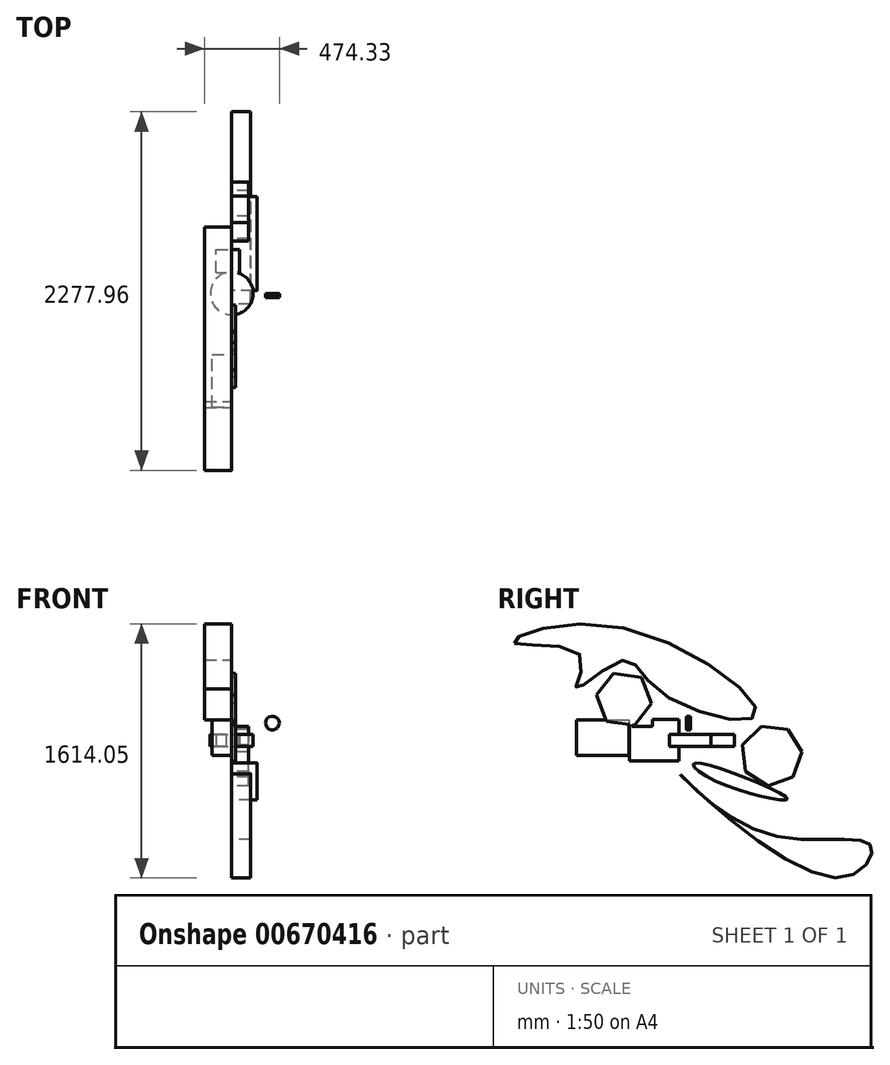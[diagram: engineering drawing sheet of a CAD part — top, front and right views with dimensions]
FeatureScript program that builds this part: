
annotation { "Feature Type Name" : "Feature", "Feature Type Description" : "" }
export const myFeature = defineFeature(function(context is Context, id is Id, definition is map)
    precondition{}
    {
        {
            var Q0;
            Q0=qCreatedBy(makeId("Top.planeOp"),FACE);
            var sketch = newSketch(context, id + "F0", { "sketchPlane" : qUnion([Q0])});
            skCircle(sketch, "E0", {"center": v(0, 0) * mm, "radius": 136.41 * mm});
            skLineSegment(sketch, "E1.bottom", {"start": v(-99.12, 131) * mm, "end": v(49.66, 131) * mm});
            skLineSegment(sketch, "E1.top", {"start": v(-99.12, 278.74) * mm, "end": v(49.66, 278.74) * mm});
            skLineSegment(sketch, "E1.left", {"start": v(-99.12, 131) * mm, "end": v(-99.12, 278.74) * mm});
            skLineSegment(sketch, "E1.right", {"start": v(49.66, 131) * mm, "end": v(49.66, 278.74) * mm});
            skSolve(sketch);
        }
        {
            var Q0;
            Q0=makeQuery(id+"F0.imprint","IMPRINT",FACE,{"disambiguationData":[TD([[makeQuery(id+"F0.imprint","IMPRINT",EDGE,{"derivedFrom":sQuery(id+"F0.wireOp",EDGE,"E1.top")}),-1.0]])]});
            var Q1;
            {var subQ0=sQuery(id+"F0.wireOp",EDGE,"E1.bottom");var subQ1=sQuery(id+"F0.wireOp",EDGE,"E0");var subQ2=makeQuery(id+"F0.imprint","INTERSECT",VERTEX,{"disambiguationData":[OD(0.0)],"derivedFrom":[subQ1,subQ0]});Q1=makeQuery(id+"F0.imprint","IMPRINT",FACE,{"disambiguationData":[TD([[makeQuery(id+"F0.imprint","IMPRINT",EDGE,{"disambiguationData":[TD([[subQ2,1.0]])],"derivedFrom":subQ1}),1.0]])]});}
            var Q2;
            {var subQ0=sQuery(id+"F0.wireOp",EDGE,"E1.bottom");var subQ1=sQuery(id+"F0.wireOp",EDGE,"E0");var subQ2=makeQuery(id+"F0.imprint","INTERSECT",VERTEX,{"disambiguationData":[OD(0.0)],"derivedFrom":[subQ1,subQ0]});Q2=makeQuery(id+"F0.imprint","IMPRINT",FACE,{"disambiguationData":[TD([[makeQuery(id+"F0.imprint","IMPRINT",EDGE,{"disambiguationData":[TD([[subQ2,-1.0]])],"derivedFrom":subQ1}),1.0]])]});}
            extrude(context, id + "F1", {"entities" : qUnion([Q0, Q1, Q2]), "depth" : 76.2 * mm, "offsetDistance" : 25.4 * mm});
        }
        {
            var Q0;
            Q0=qCreatedBy(makeId("Right.planeOp"),FACE);
            var sketch = newSketch(context, id + "F2", { "sketchPlane" : qUnion([Q0])});
            skLineSegment(sketch, "E2.bottom", {"start": v(-240.28, 128.57) * mm, "end": v(-370.37, 128.57) * mm});
            skLineSegment(sketch, "E2.top", {"start": v(-240.28, 215.65) * mm, "end": v(-370.37, 215.65) * mm});
            skLineSegment(sketch, "E2.left", {"start": v(-240.28, 128.57) * mm, "end": v(-240.28, 215.65) * mm});
            skLineSegment(sketch, "E2.right", {"start": v(-370.37, 128.57) * mm, "end": v(-370.37, 215.65) * mm});
            skLineSegment(sketch, "E3.bottom", {"start": v(-73.44, -92) * mm, "end": v(-385.92, -92) * mm});
            skLineSegment(sketch, "E3.top", {"start": v(-73.44, 172) * mm, "end": v(-385.92, 172) * mm});
            skLineSegment(sketch, "E3.left", {"start": v(-73.44, -92) * mm, "end": v(-73.44, 172) * mm});
            skLineSegment(sketch, "E3.right", {"start": v(-385.92, -92) * mm, "end": v(-385.92, 172) * mm});
            skSolve(sketch);
        }
        {
            var Q0;
            {var subQ1=sQuery(id+"F2.wireOp",EDGE,"E2.bottom");Q0=makeQuery(id+"F2.imprint","IMPRINT",FACE,{"disambiguationData":[TD([[makeQuery(id+"F2.imprint","IMPRINT",EDGE,{"derivedFrom":subQ1}),1.0]])]});}
            extrude(context, id + "F3", {"entities" : qUnion([Q0]), "operationType" : NewBodyOperationType.ADD, "depth" : 25.4 * mm, "offsetDistance" : 25.4 * mm});
        }
        {
            var Q0;
            Q0=qCreatedBy(makeId("Front.planeOp"),FACE);
            var sketch = newSketch(context, id + "F4", { "sketchPlane" : qUnion([Q0])});
            skCircle(sketch, "E4.cCircle", {"center": v(257.8, 149.5) * mm, "radius": 43.18 * mm, "construction": true});
            skLineSegment(sketch, "E4.0", {"start": v(267.09, 192.35) * mm, "end": v(281.18, 186.59) * mm});
            skLineSegment(sketch, "E4.1", {"start": v(281.18, 186.59) * mm, "end": v(292.46, 176.35) * mm});
            skLineSegment(sketch, "E4.2", {"start": v(292.46, 176.35) * mm, "end": v(299.55, 162.88) * mm});
            skLineSegment(sketch, "E4.3", {"start": v(299.55, 162.88) * mm, "end": v(301.61, 147.8) * mm});
            skLineSegment(sketch, "E4.4", {"start": v(301.61, 147.8) * mm, "end": v(298.38, 132.9) * mm});
            skLineSegment(sketch, "E4.5", {"start": v(298.38, 132.9) * mm, "end": v(290.26, 120.03) * mm});
            skLineSegment(sketch, "E4.6", {"start": v(290.26, 120.03) * mm, "end": v(278.22, 110.7) * mm});
            skLineSegment(sketch, "E4.7", {"start": v(278.22, 110.7) * mm, "end": v(263.72, 106.05) * mm});
            skLineSegment(sketch, "E4.8", {"start": v(263.72, 106.05) * mm, "end": v(248.5, 106.65) * mm});
            skLineSegment(sketch, "E4.9", {"start": v(248.5, 106.65) * mm, "end": v(234.4, 112.4) * mm});
            skLineSegment(sketch, "E4.10", {"start": v(234.4, 112.4) * mm, "end": v(223.13, 122.64) * mm});
            skLineSegment(sketch, "E4.11", {"start": v(223.13, 122.64) * mm, "end": v(216.04, 136.12) * mm});
            skLineSegment(sketch, "E4.12", {"start": v(216.04, 136.12) * mm, "end": v(213.98, 151.2) * mm});
            skLineSegment(sketch, "E4.13", {"start": v(213.98, 151.2) * mm, "end": v(217.2, 166.09) * mm});
            skLineSegment(sketch, "E4.14", {"start": v(217.2, 166.09) * mm, "end": v(225.33, 178.97) * mm});
            skLineSegment(sketch, "E4.15", {"start": v(225.33, 178.97) * mm, "end": v(237.37, 188.3) * mm});
            skLineSegment(sketch, "E4.16", {"start": v(237.37, 188.3) * mm, "end": v(251.87, 192.94) * mm});
            skLineSegment(sketch, "E4.17", {"start": v(251.87, 192.94) * mm, "end": v(267.09, 192.35) * mm});
            skPoint(sketch, "E4.0.midPoint", {"position": v(274.13, 189.47) * mm});
            skCircle(sketch, "E5.cCircle", {"center": v(257.8, 149.5) * mm, "radius": 56.72 * mm, "construction": true});
            skLineSegment(sketch, "E5.0", {"start": v(225.4, 101.87) * mm, "end": v(211.07, 115.82) * mm});
            skLineSegment(sketch, "E5.1", {"start": v(211.07, 115.82) * mm, "end": v(202.37, 133.83) * mm});
            skLineSegment(sketch, "E5.2", {"start": v(202.37, 133.83) * mm, "end": v(200.35, 153.73) * mm});
            skLineSegment(sketch, "E5.3", {"start": v(200.35, 153.73) * mm, "end": v(205.27, 173.12) * mm});
            skLineSegment(sketch, "E5.4", {"start": v(205.27, 173.12) * mm, "end": v(216.51, 189.66) * mm});
            skLineSegment(sketch, "E5.5", {"start": v(216.51, 189.66) * mm, "end": v(232.74, 201.36) * mm});
            skLineSegment(sketch, "E5.6", {"start": v(232.74, 201.36) * mm, "end": v(251.99, 206.8) * mm});
            skLineSegment(sketch, "E5.7", {"start": v(251.99, 206.8) * mm, "end": v(271.94, 205.33) * mm});
            skLineSegment(sketch, "E5.8", {"start": v(271.94, 205.33) * mm, "end": v(290.18, 197.13) * mm});
            skLineSegment(sketch, "E5.9", {"start": v(290.18, 197.13) * mm, "end": v(304.52, 183.18) * mm});
            skLineSegment(sketch, "E5.10", {"start": v(304.52, 183.18) * mm, "end": v(313.22, 165.17) * mm});
            skLineSegment(sketch, "E5.11", {"start": v(313.22, 165.17) * mm, "end": v(315.24, 145.27) * mm});
            skLineSegment(sketch, "E5.12", {"start": v(315.24, 145.27) * mm, "end": v(310.33, 125.87) * mm});
            skLineSegment(sketch, "E5.13", {"start": v(310.33, 125.87) * mm, "end": v(299.08, 109.33) * mm});
            skLineSegment(sketch, "E5.14", {"start": v(299.08, 109.33) * mm, "end": v(282.85, 97.64) * mm});
            skLineSegment(sketch, "E5.15", {"start": v(282.85, 97.64) * mm, "end": v(263.6, 92.2) * mm});
            skLineSegment(sketch, "E5.16", {"start": v(263.6, 92.2) * mm, "end": v(243.65, 93.66) * mm});
            skLineSegment(sketch, "E5.17", {"start": v(243.65, 93.66) * mm, "end": v(225.4, 101.87) * mm});
            skPoint(sketch, "E5.0.midPoint", {"position": v(218.24, 108.84) * mm});
            skCircle(sketch, "E6.cCircle", {"center": v(257.8, 149.5) * mm, "radius": 97.4 * mm, "construction": true});
            skPoint(sketch, "E6.cCircle.perimeterSnap0", {"position": v(228.77, 117.52) * mm});
            skLineSegment(sketch, "E6.0", {"start": v(169.04, 108.17) * mm, "end": v(162.54, 126.88) * mm});
            skLineSegment(sketch, "E6.1", {"start": v(162.54, 126.88) * mm, "end": v(159.93, 146.52) * mm});
            skLineSegment(sketch, "E6.2", {"start": v(159.93, 146.52) * mm, "end": v(161.34, 166.28) * mm});
            skLineSegment(sketch, "E6.3", {"start": v(161.34, 166.28) * mm, "end": v(166.69, 185.35) * mm});
            skLineSegment(sketch, "E6.4", {"start": v(166.69, 185.35) * mm, "end": v(175.77, 202.96) * mm});
            skLineSegment(sketch, "E6.5", {"start": v(175.77, 202.96) * mm, "end": v(188.21, 218.38) * mm});
            skLineSegment(sketch, "E6.6", {"start": v(188.21, 218.38) * mm, "end": v(203.5, 230.97) * mm});
            skLineSegment(sketch, "E6.7", {"start": v(203.5, 230.97) * mm, "end": v(221.01, 240.24) * mm});
            skLineSegment(sketch, "E6.8", {"start": v(221.01, 240.24) * mm, "end": v(240.03, 245.78) * mm});
            skLineSegment(sketch, "E6.9", {"start": v(240.03, 245.78) * mm, "end": v(259.78, 247.39) * mm});
            skLineSegment(sketch, "E6.10", {"start": v(259.78, 247.39) * mm, "end": v(279.44, 244.98) * mm});
            skLineSegment(sketch, "E6.11", {"start": v(279.44, 244.98) * mm, "end": v(298.22, 238.67) * mm});
            skLineSegment(sketch, "E6.12", {"start": v(298.22, 238.67) * mm, "end": v(315.34, 228.7) * mm});
            skLineSegment(sketch, "E6.13", {"start": v(315.34, 228.7) * mm, "end": v(330.11, 215.5) * mm});
            skLineSegment(sketch, "E6.14", {"start": v(330.11, 215.5) * mm, "end": v(341.92, 199.6) * mm});
            skLineSegment(sketch, "E6.15", {"start": v(341.92, 199.6) * mm, "end": v(350.28, 181.64) * mm});
            skLineSegment(sketch, "E6.16", {"start": v(350.28, 181.64) * mm, "end": v(354.86, 162.36) * mm});
            skLineSegment(sketch, "E6.17", {"start": v(354.86, 162.36) * mm, "end": v(355.46, 142.56) * mm});
            skLineSegment(sketch, "E6.18", {"start": v(355.46, 142.56) * mm, "end": v(352.06, 123.04) * mm});
            skLineSegment(sketch, "E6.19", {"start": v(352.06, 123.04) * mm, "end": v(344.8, 104.6) * mm});
            skLineSegment(sketch, "E6.20", {"start": v(344.8, 104.6) * mm, "end": v(334, 88.01) * mm});
            skLineSegment(sketch, "E6.21", {"start": v(334, 88.01) * mm, "end": v(320.05, 73.93) * mm});
            skLineSegment(sketch, "E6.22", {"start": v(320.05, 73.93) * mm, "end": v(303.57, 62.95) * mm});
            skLineSegment(sketch, "E6.23", {"start": v(303.57, 62.95) * mm, "end": v(285.2, 55.5) * mm});
            skLineSegment(sketch, "E6.24", {"start": v(285.2, 55.5) * mm, "end": v(265.73, 51.91) * mm});
            skLineSegment(sketch, "E6.25", {"start": v(265.73, 51.91) * mm, "end": v(245.92, 52.31) * mm});
            skLineSegment(sketch, "E6.26", {"start": v(245.92, 52.31) * mm, "end": v(226.6, 56.7) * mm});
            skLineSegment(sketch, "E6.27", {"start": v(226.6, 56.7) * mm, "end": v(208.56, 64.87) * mm});
            skLineSegment(sketch, "E6.28", {"start": v(208.56, 64.87) * mm, "end": v(192.53, 76.52) * mm});
            skLineSegment(sketch, "E6.29", {"start": v(192.53, 76.52) * mm, "end": v(179.17, 91.15) * mm});
            skLineSegment(sketch, "E6.30", {"start": v(179.17, 91.15) * mm, "end": v(169.04, 108.17) * mm});
            skPoint(sketch, "E6.0.midPoint", {"position": v(165.79, 117.52) * mm});
            skPoint(sketch, "E6.0.midPoint.positionSnap0", {"position": v(228.77, 117.52) * mm});
            skSolve(sketch);
        }
        {
            var Q0;
            Q0=makeQuery(id+"F4.imprint","IMPRINT",FACE,{"disambiguationData":[TD([[makeQuery(id+"F4.imprint","IMPRINT",EDGE,{"derivedFrom":sQuery(id+"F4.wireOp",EDGE,"E4.0")}),-1.0]])]});
            extrude(context, id + "F5", {"entities" : qUnion([Q0]), "depth" : 25.4 * mm, "offsetDistance" : 25.4 * mm});
        }
        {
            var Q0;
            Q0=qCreatedBy(makeId("Right.planeOp"),FACE);
            var sketch = newSketch(context, id + "F6", { "sketchPlane" : qUnion([Q0])});
            skFitSpline(sketch, "E7", {"points": [v(32.47, -104.53) * mm, v(156.08, -216.22) * mm, v(614.82, -326.92) * mm, v(32.47, -104.53) * mm]});
            skSolve(sketch);
        }
        {
            var Q0;
            Q0 = qSketchRegion(id + "F6", true);
            extrude(context, id + "F7", {"entities" : qUnion([Q0]), "depth" : 161.54 * mm, "offsetDistance" : 25.4 * mm});
        }
        {
            var Q0;
            Q0=qCreatedBy(makeId("Right.planeOp"),FACE);
            var sketch = newSketch(context, id + "F8", { "sketchPlane" : qUnion([Q0])});
            skCircle(sketch, "E8.cCircle", {"center": v(-421.8, 300.6) * mm, "radius": 153.91 * mm, "construction": true});
            skLineSegment(sketch, "E8.0", {"start": v(-245.98, 274.67) * mm, "end": v(-356.34, 135.37) * mm});
            skLineSegment(sketch, "E8.1", {"start": v(-356.34, 135.37) * mm, "end": v(-532.16, 161.3) * mm});
            skLineSegment(sketch, "E8.2", {"start": v(-532.16, 161.3) * mm, "end": v(-597.62, 326.52) * mm});
            skLineSegment(sketch, "E8.3", {"start": v(-597.62, 326.52) * mm, "end": v(-487.26, 465.83) * mm});
            skLineSegment(sketch, "E8.4", {"start": v(-487.26, 465.83) * mm, "end": v(-311.44, 439.9) * mm});
            skLineSegment(sketch, "E8.5", {"start": v(-311.44, 439.9) * mm, "end": v(-245.98, 274.67) * mm});
            skPoint(sketch, "E8.0.midPoint", {"position": v(-301.16, 205.02) * mm});
            skSolve(sketch);
        }
        {
            var Q0;
            Q0=makeQuery(id+"F8.imprint","IMPRINT",FACE,{"disambiguationData":[TD([[makeQuery(id+"F8.imprint","IMPRINT",EDGE,{"derivedFrom":sQuery(id+"F8.wireOp",EDGE,"E8.0")}),-1.0]])]});
            extrude(context, id + "F9", {"entities" : qUnion([Q0]), "operationType" : NewBodyOperationType.ADD, "depth" : 25.4 * mm, "offsetDistance" : 25.4 * mm});
        }
        {
            var Q0;
            Q0=qCreatedBy(makeId("Right.planeOp"),FACE);
            var sketch = newSketch(context, id + "F10", { "sketchPlane" : qUnion([Q0])});
            skFitSpline(sketch, "E9", {"points": [v(-64.42, -177.48) * mm, v(498.17, -556.76) * mm, v(1146.78, -631.42) * mm, v(923.6, -833.9) * mm, v(-69.07, -173.82) * mm, v(-64.42, -177.48) * mm]});
            skSolve(sketch);
        }
        {
            var Q0;
            Q0=makeQuery(id+"F10.imprint","IMPRINT",FACE,{"disambiguationData":[TD([[makeQuery(id+"F10.imprint","IMPRINT",EDGE,{"derivedFrom":sQuery(id+"F10.wireOp",EDGE,"E9")}),-1.0]])]});
            extrude(context, id + "F11", {"entities" : qUnion([Q0]), "depth" : 119.38 * mm, "offsetDistance" : 25.4 * mm});
        }
        {
            var Q0;
            Q0=qCreatedBy(makeId("Right.planeOp"),FACE);
            var sketch = newSketch(context, id + "F12", { "sketchPlane" : qUnion([Q0])});
            skCircle(sketch, "E10.cCircle", {"center": v(514.44, -54.86) * mm, "radius": 194.84 * mm, "construction": true});
            skLineSegment(sketch, "E10.0", {"start": v(651.6, -193.24) * mm, "end": v(491.78, -248.37) * mm});
            skLineSegment(sketch, "E10.1", {"start": v(491.78, -248.37) * mm, "end": v(349.02, -157.8) * mm});
            skLineSegment(sketch, "E10.2", {"start": v(349.02, -157.8) * mm, "end": v(330.83, 10.3) * mm});
            skLineSegment(sketch, "E10.3", {"start": v(330.83, 10.3) * mm, "end": v(450.9, 129.32) * mm});
            skLineSegment(sketch, "E10.4", {"start": v(450.9, 129.32) * mm, "end": v(618.83, 109.65) * mm});
            skLineSegment(sketch, "E10.5", {"start": v(618.83, 109.65) * mm, "end": v(708.15, -33.9) * mm});
            skLineSegment(sketch, "E10.6", {"start": v(708.15, -33.9) * mm, "end": v(651.6, -193.24) * mm});
            skSolve(sketch);
        }
        {
            var Q0;
            Q0=makeQuery(id+"F12.imprint","IMPRINT",FACE,{"disambiguationData":[TD([[makeQuery(id+"F12.imprint","IMPRINT",EDGE,{"derivedFrom":sQuery(id+"F12.wireOp",EDGE,"E10.0")}),-1.0]])]});
            extrude(context, id + "F13", {"entities" : qUnion([Q0]), "depth" : 106.68 * mm, "offsetDistance" : 25.4 * mm});
        }
        {
            var Q0;
            Q0=qCreatedBy(makeId("Right.planeOp"),FACE);
            var sketch = newSketch(context, id + "F14", { "sketchPlane" : qUnion([Q0])});
            skLineSegment(sketch, "E11.bottom", {"start": v(-722.33, 168.92) * mm, "end": v(-389.89, 168.92) * mm});
            skLineSegment(sketch, "E11.top", {"start": v(-722.33, -55.02) * mm, "end": v(-389.89, -55.02) * mm});
            skLineSegment(sketch, "E11.left", {"start": v(-722.33, 168.92) * mm, "end": v(-722.33, -55.02) * mm});
            skLineSegment(sketch, "E11.right", {"start": v(-389.89, 168.92) * mm, "end": v(-389.89, -55.02) * mm});
            skSolve(sketch);
        }
        {
            var Q0;
            Q0=makeQuery(id+"F14.imprint","IMPRINT",FACE,{"disambiguationData":[TD([[makeQuery(id+"F14.imprint","IMPRINT",EDGE,{"derivedFrom":sQuery(id+"F14.wireOp",EDGE,"E11.bottom")}),-1.0]])]});
            extrude(context, id + "F15", {"entities" : qUnion([Q0]), "operationType" : NewBodyOperationType.ADD, "oppositeDirection" : true, "depth" : 124.46 * mm, "offsetDistance" : 25.4 * mm});
        }
        {
            var Q0;
            Q0=qCreatedBy(makeId("Right.planeOp"),FACE);
            var sketch = newSketch(context, id + "F16", { "sketchPlane" : qUnion([Q0])});
            skFitSpline(sketch, "E12", {"points": [v(-1116.7, 656.66) * mm, v(-500.36, 766.92) * mm, v(416.42, 197.66) * mm, v(-193.73, 348.95) * mm, v(-432.22, 548.66) * mm, v(-723.36, 368.79) * mm, v(-698.58, 579.92) * mm, v(-1116.7, 656.66) * mm]});
            skSolve(sketch);
        }
        {
            var Q0;
            Q0=makeQuery(id+"F16.imprint","IMPRINT",FACE,{"disambiguationData":[TD([[makeQuery(id+"F16.imprint","IMPRINT",EDGE,{"derivedFrom":sQuery(id+"F16.wireOp",EDGE,"E12")}),-1.0]])]});
            extrude(context, id + "F17", {"entities" : qUnion([Q0]), "oppositeDirection" : true, "depth" : 172.72 * mm, "offsetDistance" : 25.4 * mm});
        }
    });
